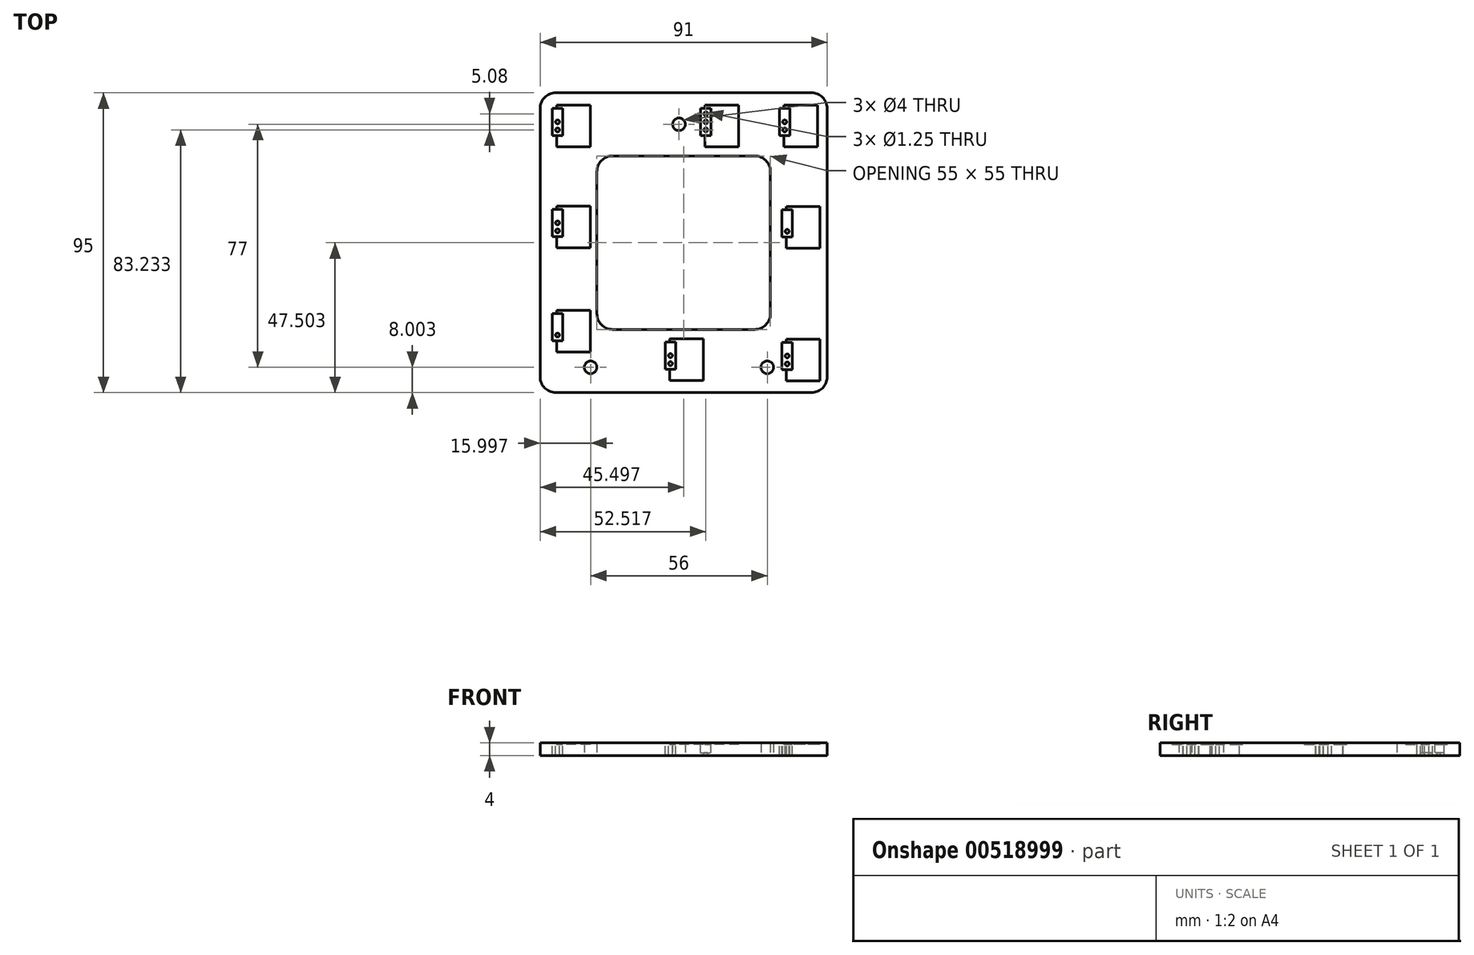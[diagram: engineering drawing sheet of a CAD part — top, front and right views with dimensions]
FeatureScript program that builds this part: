
annotation { "Feature Type Name" : "Feature", "Feature Type Description" : "" }
export const myFeature = defineFeature(function(context is Context, id is Id, definition is map)
    precondition{}
    {
        {
            var Q0;
            Q0=qCreatedBy(makeId("Top.planeOp"),FACE);
            var sketch = newSketch(context, id + "F0", { "sketchPlane" : qUnion([Q0])});
            skLineSegment(sketch, "E0.bottom", {"start": v(-14.66, 9.36) * mm, "end": v(40.34, 9.36) * mm});
            skLineSegment(sketch, "E0.top", {"start": v(-14.66, -45.64) * mm, "end": v(40.34, -45.64) * mm});
            skLineSegment(sketch, "E0.left", {"start": v(-14.66, 9.36) * mm, "end": v(-14.66, -45.64) * mm});
            skLineSegment(sketch, "E0.right", {"start": v(40.34, 9.36) * mm, "end": v(40.34, -45.64) * mm});
            skLineSegment(sketch, "E1.bottom", {"start": v(-32.66, 29.36) * mm, "end": v(58.34, 29.36) * mm});
            skLineSegment(sketch, "E1.top", {"start": v(-32.66, -65.64) * mm, "end": v(58.34, -65.64) * mm});
            skLineSegment(sketch, "E1.left", {"start": v(-32.66, 29.36) * mm, "end": v(-32.66, -65.64) * mm});
            skLineSegment(sketch, "E1.right", {"start": v(58.34, 29.36) * mm, "end": v(58.34, -65.64) * mm});
            skLineSegment(sketch, "E2", {"start": v(40.34, 13.7) * mm, "end": v(58.34, 13.7) * mm, "construction": true});
            skLineSegment(sketch, "E3", {"start": v(-14.66, -14.15) * mm, "end": v(-32.66, -14.15) * mm, "construction": true});
            skLineSegment(sketch, "E4", {"start": v(9.38, 9.36) * mm, "end": v(9.38, 29.36) * mm, "construction": true});
            skLineSegment(sketch, "E5", {"start": v(10.46, -65.64) * mm, "end": v(10.46, -45.64) * mm, "construction": true});
            skCircle(sketch, "E6", {"center": v(11.34, 19.36) * mm, "radius": 2 * mm});
            skCircle(sketch, "E7", {"center": v(39.34, -57.64) * mm, "radius": 2 * mm});
            skCircle(sketch, "E8", {"center": v(-16.66, -57.64) * mm, "radius": 2 * mm});
            skLineSegment(sketch, "E9", {"start": v(39.34, -57.64) * mm, "end": v(-16.66, -57.64) * mm, "construction": true});
            skLineSegment(sketch, "E10", {"start": v(11.34, 19.36) * mm, "end": v(11.34, 29.36) * mm, "construction": true});
            skLineSegment(sketch, "E11", {"start": v(11.34, 19.36) * mm, "end": v(11.34, 9.36) * mm, "construction": true});
            skLineSegment(sketch, "E12", {"start": v(39.34, -57.64) * mm, "end": v(58.34, -57.64) * mm, "construction": true});
            skSolve(sketch);
        }
        {
            var Q0;
            Q0=makeQuery(id+"F0.imprint","IMPRINT",FACE,{"disambiguationData":[TD([[makeQuery(id+"F0.imprint","IMPRINT",EDGE,{"derivedFrom":sQuery(id+"F0.wireOp",EDGE,"E0.bottom")}),1.0]])]});
            extrude(context, id + "F1", {"entities" : qUnion([Q0]), "depth" : 4 * mm, "offsetDistance" : 25 * mm});
        }
        {
            var Q0;
            Q0=makeQuery(id+"F1.opExtrude","CAP_FACE",FACE,{"disambiguationData":[OSD([sQuery(id+"F0.wireOp",EDGE,"E0.bottom"),sQuery(id+"F0.wireOp",EDGE,"E0.top"),sQuery(id+"F0.wireOp",EDGE,"E0.left"),sQuery(id+"F0.wireOp",EDGE,"E0.right"),sQuery(id+"F0.wireOp",EDGE,"E1.bottom"),sQuery(id+"F0.wireOp",EDGE,"E1.top"),sQuery(id+"F0.wireOp",EDGE,"E1.left"),sQuery(id+"F0.wireOp",EDGE,"E1.right")])],"isStart":false});
            var sketch = newSketch(context, id + "F2", { "sketchPlane" : qUnion([Q0])});
            skPoint(sketch, "E13", {"position": v(49.94, 18.86) * mm});
            skLineSegment(sketch, "E14", {"start": v(49.94, 18.86) * mm, "end": v(49.94, 9.36) * mm, "construction": true});
            skLineSegment(sketch, "E15.bottom", {"start": v(55.27, 12.26) * mm, "end": v(44.6, 12.26) * mm});
            skLineSegment(sketch, "E15.top", {"start": v(55.27, 25.47) * mm, "end": v(44.6, 25.47) * mm});
            skLineSegment(sketch, "E15.left", {"start": v(55.27, 12.26) * mm, "end": v(55.27, 25.47) * mm});
            skLineSegment(sketch, "E15.right", {"start": v(44.6, 12.26) * mm, "end": v(44.6, 25.47) * mm});
            skLineSegment(sketch, "E16.bottom", {"start": v(43.2, 24.45) * mm, "end": v(46.5, 24.45) * mm});
            skLineSegment(sketch, "E16.top", {"start": v(43.2, 15.81) * mm, "end": v(46.5, 15.81) * mm});
            skLineSegment(sketch, "E16.left", {"start": v(43.2, 24.45) * mm, "end": v(43.2, 15.81) * mm});
            skLineSegment(sketch, "E16.right", {"start": v(46.5, 24.45) * mm, "end": v(46.5, 15.81) * mm});
            skPoint(sketch, "E17", {"position": v(55.02, 22.67) * mm});
            skPoint(sketch, "E18", {"position": v(52.48, 25.21) * mm});
            skPoint(sketch, "E19", {"position": v(47.4, 25.21) * mm});
            skPoint(sketch, "E20", {"position": v(55.02, 20.13) * mm});
            skPoint(sketch, "E21", {"position": v(55.02, 17.6) * mm});
            skPoint(sketch, "E22", {"position": v(52.48, 12.51) * mm});
            skPoint(sketch, "E23", {"position": v(47.4, 12.51) * mm});
            skPoint(sketch, "E24", {"position": v(44.86, 17.6) * mm});
            skPoint(sketch, "E25", {"position": v(44.86, 22.67) * mm});
            skPoint(sketch, "E26", {"position": v(44.86, 20.13) * mm});
            skLineSegment(sketch, "E27", {"start": v(55.02, 17.6) * mm, "end": v(55.02, 20.13) * mm, "construction": true});
            skLineSegment(sketch, "E28", {"start": v(55.02, 22.67) * mm, "end": v(55.02, 20.13) * mm, "construction": true});
            skLineSegment(sketch, "E29", {"start": v(52.48, 12.51) * mm, "end": v(47.4, 12.51) * mm, "construction": true});
            skLineSegment(sketch, "E30", {"start": v(47.4, 25.21) * mm, "end": v(52.48, 25.21) * mm, "construction": true});
            skLineSegment(sketch, "E31", {"start": v(44.86, 20.13) * mm, "end": v(44.86, 17.6) * mm, "construction": true});
            skLineSegment(sketch, "E32", {"start": v(44.86, 22.67) * mm, "end": v(44.86, 20.13) * mm, "construction": true});
            skLineSegment(sketch, "E33", {"start": v(49.94, 25.21) * mm, "end": v(49.94, 25.47) * mm, "construction": true});
            skPoint(sketch, "E34", {"position": v(44.86, 15.05) * mm});
            skPoint(sketch, "E35", {"position": v(55.02, 15.05) * mm});
            skLineSegment(sketch, "E36", {"start": v(44.86, 17.6) * mm, "end": v(44.86, 15.05) * mm, "construction": true});
            skLineSegment(sketch, "E37", {"start": v(55.02, 17.6) * mm, "end": v(55.02, 15.05) * mm, "construction": true});
            skLineSegment(sketch, "E38", {"start": v(44.86, 18.86) * mm, "end": v(44.6, 18.86) * mm, "construction": true});
            skLineSegment(sketch, "E39", {"start": v(44.86, 22.67) * mm, "end": v(46.5, 22.67) * mm, "construction": true});
            skLineSegment(sketch, "E40", {"start": v(44.86, 22.67) * mm, "end": v(44.86, 24.45) * mm, "construction": true});
            skPoint(sketch, "E40.endSnap0", {"position": v(44.86, 24.45) * mm});
            skLineSegment(sketch, "E41", {"start": v(44.86, 22.67) * mm, "end": v(43.2, 22.67) * mm, "construction": true});
            skCircle(sketch, "E42", {"center": v(44.86, 22.67) * mm, "radius": 0.62 * mm});
            skCircle(sketch, "E43", {"center": v(44.86, 20.13) * mm, "radius": 0.62 * mm});
            skCircle(sketch, "E44", {"center": v(44.86, 17.6) * mm, "radius": 0.62 * mm});
            skLineSegment(sketch, "E45", {"start": v(44.86, 17.6) * mm, "end": v(46.5, 17.6) * mm, "construction": true});
            skLineSegment(sketch, "E46.1.0.0", {"start": v(30.27, 25.47) * mm, "end": v(19.6, 25.47) * mm});
            skLineSegment(sketch, "E46.1.0.1", {"start": v(18.2, 24.45) * mm, "end": v(21.5, 24.45) * mm});
            skCircle(sketch, "E46.1.0.2", {"center": v(19.86, 20.13) * mm, "radius": 0.62 * mm});
            skCircle(sketch, "E46.1.0.3", {"center": v(19.86, 22.67) * mm, "radius": 0.62 * mm});
            skCircle(sketch, "E46.1.0.4", {"center": v(19.86, 17.6) * mm, "radius": 0.62 * mm});
            skLineSegment(sketch, "E46.1.0.5", {"start": v(18.2, 24.45) * mm, "end": v(18.2, 15.81) * mm});
            skLineSegment(sketch, "E46.1.0.6", {"start": v(18.2, 15.81) * mm, "end": v(21.5, 15.81) * mm});
            skLineSegment(sketch, "E46.1.0.7", {"start": v(21.5, 24.45) * mm, "end": v(21.5, 15.81) * mm});
            skLineSegment(sketch, "E46.1.0.8", {"start": v(19.6, 12.26) * mm, "end": v(19.6, 25.47) * mm});
            skLineSegment(sketch, "E46.1.0.9", {"start": v(30.27, 12.26) * mm, "end": v(19.6, 12.26) * mm});
            skLineSegment(sketch, "E46.1.0.10", {"start": v(30.27, 12.26) * mm, "end": v(30.27, 25.47) * mm});
            skLineSegment(sketch, "E46.direction1", {"start": v(44.6, 12.26) * mm, "end": v(19.6, 12.26) * mm, "construction": true});
            skLineSegment(sketch, "E47.1.0.0", {"start": v(-28.8, 24.45) * mm, "end": v(-28.8, 15.81) * mm});
            skLineSegment(sketch, "E47.1.0.1", {"start": v(-27.4, 12.26) * mm, "end": v(-27.4, 25.47) * mm});
            skLineSegment(sketch, "E47.1.0.2", {"start": v(-28.8, 24.45) * mm, "end": v(-25.5, 24.45) * mm});
            skLineSegment(sketch, "E47.1.0.3", {"start": v(-16.73, 12.26) * mm, "end": v(-16.73, 25.47) * mm});
            skLineSegment(sketch, "E47.1.0.4", {"start": v(-28.8, 15.81) * mm, "end": v(-25.5, 15.81) * mm});
            skLineSegment(sketch, "E47.1.0.5", {"start": v(-25.5, 24.45) * mm, "end": v(-25.5, 15.81) * mm});
            skLineSegment(sketch, "E47.1.0.6", {"start": v(-16.73, 25.47) * mm, "end": v(-27.4, 25.47) * mm});
            skLineSegment(sketch, "E47.1.0.7", {"start": v(-16.73, 12.26) * mm, "end": v(-27.4, 12.26) * mm});
            skCircle(sketch, "E47.1.0.8", {"center": v(-27.14, 17.6) * mm, "radius": 0.62 * mm});
            skCircle(sketch, "E47.1.0.9", {"center": v(-27.14, 22.67) * mm, "radius": 0.62 * mm});
            skCircle(sketch, "E47.1.0.10", {"center": v(-27.14, 20.13) * mm, "radius": 0.62 * mm});
            skLineSegment(sketch, "E47.direction1", {"start": v(19.6, 12.26) * mm, "end": v(-27.4, 12.26) * mm, "construction": true});
            skLineSegment(sketch, "E48", {"start": v(49.94, 18.86) * mm, "end": v(58.34, 18.86) * mm, "construction": true});
            skLineSegment(sketch, "E49.0.1.0", {"start": v(-25.5, -7.54) * mm, "end": v(-25.5, -16.17) * mm});
            skLineSegment(sketch, "E49.0.1.1", {"start": v(-16.73, -19.73) * mm, "end": v(-16.73, -6.52) * mm});
            skLineSegment(sketch, "E49.0.1.2", {"start": v(-16.73, -6.52) * mm, "end": v(-27.4, -6.52) * mm});
            skLineSegment(sketch, "E49.0.1.3", {"start": v(-28.8, -16.17) * mm, "end": v(-25.5, -16.17) * mm});
            skLineSegment(sketch, "E49.0.1.4", {"start": v(-16.73, -19.73) * mm, "end": v(-27.4, -19.73) * mm});
            skLineSegment(sketch, "E49.0.1.5", {"start": v(-27.4, -19.73) * mm, "end": v(-27.4, -6.52) * mm});
            skLineSegment(sketch, "E49.0.1.6", {"start": v(-28.8, -7.54) * mm, "end": v(-28.8, -16.17) * mm});
            skCircle(sketch, "E49.0.1.7", {"center": v(-27.14, -9.32) * mm, "radius": 0.62 * mm});
            skCircle(sketch, "E49.0.1.8", {"center": v(-27.14, -14.4) * mm, "radius": 0.62 * mm});
            skCircle(sketch, "E49.0.1.9", {"center": v(-27.14, -11.86) * mm, "radius": 0.62 * mm});
            skLineSegment(sketch, "E49.0.1.10", {"start": v(-28.8, -7.54) * mm, "end": v(-25.5, -7.54) * mm});
            skLineSegment(sketch, "E49.direction1", {"start": v(-26.4, 12.26) * mm, "end": v(-7.4, 12.5) * mm, "construction": true});
            skLineSegment(sketch, "E49.direction2", {"start": v(-26.4, 12.26) * mm, "end": v(-26.4, -19.74) * mm, "construction": true});
            skLineSegment(sketch, "E50.0.1.0", {"start": v(-16.73, -52.74) * mm, "end": v(-16.73, -39.53) * mm});
            skLineSegment(sketch, "E50.0.1.1", {"start": v(-28.8, -40.55) * mm, "end": v(-28.8, -49.19) * mm});
            skLineSegment(sketch, "E50.0.1.2", {"start": v(-25.5, -40.55) * mm, "end": v(-25.5, -49.19) * mm});
            skLineSegment(sketch, "E50.0.1.3", {"start": v(-27.4, -52.74) * mm, "end": v(-27.4, -39.53) * mm});
            skLineSegment(sketch, "E50.0.1.4", {"start": v(-16.73, -39.53) * mm, "end": v(-27.4, -39.53) * mm});
            skLineSegment(sketch, "E50.0.1.5", {"start": v(-16.73, -52.74) * mm, "end": v(-27.4, -52.74) * mm});
            skCircle(sketch, "E50.0.1.6", {"center": v(-27.14, -47.4) * mm, "radius": 0.62 * mm});
            skCircle(sketch, "E50.0.1.7", {"center": v(-27.14, -42.33) * mm, "radius": 0.62 * mm});
            skCircle(sketch, "E50.0.1.8", {"center": v(-27.14, -44.87) * mm, "radius": 0.62 * mm});
            skLineSegment(sketch, "E50.0.1.9", {"start": v(-28.8, -49.19) * mm, "end": v(-25.5, -49.19) * mm});
            skLineSegment(sketch, "E50.0.1.10", {"start": v(-28.8, -40.55) * mm, "end": v(-25.5, -40.55) * mm});
            skLineSegment(sketch, "E50.direction1", {"start": v(-27.4, 12.26) * mm, "end": v(-2.4, 12.26) * mm, "construction": true});
            skLineSegment(sketch, "E50.direction2", {"start": v(-27.4, 12.26) * mm, "end": v(-27.4, -52.74) * mm, "construction": true});
            skLineSegment(sketch, "E51.1.0.0", {"start": v(7, -58.24) * mm, "end": v(10.3, -58.24) * mm});
            skLineSegment(sketch, "E51.1.0.1", {"start": v(8.4, -61.8) * mm, "end": v(8.4, -48.6) * mm});
            skLineSegment(sketch, "E51.1.0.2", {"start": v(19.07, -48.6) * mm, "end": v(8.4, -48.6) * mm});
            skLineSegment(sketch, "E51.1.0.3", {"start": v(19.07, -61.8) * mm, "end": v(8.4, -61.8) * mm});
            skLineSegment(sketch, "E51.1.0.4", {"start": v(19.07, -61.8) * mm, "end": v(19.07, -48.6) * mm});
            skLineSegment(sketch, "E51.1.0.5", {"start": v(7, -49.6) * mm, "end": v(7, -58.24) * mm});
            skLineSegment(sketch, "E51.1.0.6", {"start": v(10.3, -49.6) * mm, "end": v(10.3, -58.24) * mm});
            skCircle(sketch, "E51.1.0.7", {"center": v(8.65, -56.47) * mm, "radius": 0.62 * mm});
            skCircle(sketch, "E51.1.0.8", {"center": v(8.65, -53.93) * mm, "radius": 0.62 * mm});
            skCircle(sketch, "E51.1.0.9", {"center": v(8.65, -51.39) * mm, "radius": 0.62 * mm});
            skLineSegment(sketch, "E51.1.0.10", {"start": v(7, -49.6) * mm, "end": v(10.3, -49.6) * mm});
            skLineSegment(sketch, "E51.direction1", {"start": v(-27.4, -52.74) * mm, "end": v(8.4, -61.8) * mm, "construction": true});
            skLineSegment(sketch, "E52.1.0.0", {"start": v(56.07, -61.9) * mm, "end": v(45.4, -61.9) * mm});
            skLineSegment(sketch, "E52.1.0.1", {"start": v(44, -58.34) * mm, "end": v(47.3, -58.34) * mm});
            skLineSegment(sketch, "E52.1.0.2", {"start": v(47.3, -49.7) * mm, "end": v(47.3, -58.34) * mm});
            skLineSegment(sketch, "E52.1.0.3", {"start": v(45.4, -61.9) * mm, "end": v(45.4, -48.7) * mm});
            skLineSegment(sketch, "E52.1.0.4", {"start": v(56.07, -48.7) * mm, "end": v(45.4, -48.7) * mm});
            skLineSegment(sketch, "E52.1.0.5", {"start": v(56.07, -61.9) * mm, "end": v(56.07, -48.7) * mm});
            skLineSegment(sketch, "E52.1.0.6", {"start": v(44, -49.7) * mm, "end": v(44, -58.34) * mm});
            skCircle(sketch, "E52.1.0.7", {"center": v(45.65, -51.49) * mm, "radius": 0.62 * mm});
            skCircle(sketch, "E52.1.0.8", {"center": v(45.65, -56.57) * mm, "radius": 0.62 * mm});
            skCircle(sketch, "E52.1.0.9", {"center": v(45.65, -54.03) * mm, "radius": 0.62 * mm});
            skLineSegment(sketch, "E52.1.0.10", {"start": v(44, -49.7) * mm, "end": v(47.3, -49.7) * mm});
            skLineSegment(sketch, "E52.direction1", {"start": v(8.4, -61.8) * mm, "end": v(45.4, -61.9) * mm, "construction": true});
            skLineSegment(sketch, "E53.0.1.0", {"start": v(47.3, -7.7) * mm, "end": v(47.3, -16.34) * mm});
            skLineSegment(sketch, "E53.0.1.1", {"start": v(44, -7.7) * mm, "end": v(44, -16.34) * mm});
            skLineSegment(sketch, "E53.0.1.2", {"start": v(56.07, -19.9) * mm, "end": v(56.07, -6.7) * mm});
            skLineSegment(sketch, "E53.0.1.3", {"start": v(56.07, -6.7) * mm, "end": v(45.4, -6.7) * mm});
            skLineSegment(sketch, "E53.0.1.4", {"start": v(45.4, -19.9) * mm, "end": v(45.4, -6.7) * mm});
            skLineSegment(sketch, "E53.0.1.5", {"start": v(56.07, -19.9) * mm, "end": v(45.4, -19.9) * mm});
            skLineSegment(sketch, "E53.0.1.6", {"start": v(44, -16.34) * mm, "end": v(47.3, -16.34) * mm});
            skCircle(sketch, "E53.0.1.7", {"center": v(45.65, -9.49) * mm, "radius": 0.62 * mm});
            skCircle(sketch, "E53.0.1.8", {"center": v(45.65, -14.57) * mm, "radius": 0.62 * mm});
            skCircle(sketch, "E53.0.1.9", {"center": v(45.65, -12.03) * mm, "radius": 0.62 * mm});
            skLineSegment(sketch, "E53.0.1.10", {"start": v(44, -7.7) * mm, "end": v(47.3, -7.7) * mm});
            skLineSegment(sketch, "E53.direction1", {"start": v(45.4, -61.9) * mm, "end": v(70.4, -62) * mm, "construction": true});
            skLineSegment(sketch, "E53.direction2", {"start": v(45.4, -61.9) * mm, "end": v(45.4, -19.9) * mm, "construction": true});
            skSolve(sketch);
        }
        {
            var Q0;
            Q0 = qSketchRegion(id + "F2", true);
            extrude(context, id + "F3", {"entities" : qUnion([Q0]), "operationType" : NewBodyOperationType.REMOVE, "oppositeDirection" : true, "depth" : 0.5 * mm, "offsetDistance" : 25 * mm});
        }
        {
            var Q0;
            {var subQ5=sQuery(id+"F2.wireOp",EDGE,"E16.left");Q0=makeQuery(id+"F2.imprint","IMPRINT",FACE,{"disambiguationData":[TD([[makeQuery(id+"F2.imprint","IMPRINT",EDGE,{"derivedFrom":subQ5}),1.0]])]});}
            var Q1;
            {var subQ5=sQuery(id+"F2.wireOp",EDGE,"E16.right");Q1=makeQuery(id+"F2.imprint","IMPRINT",FACE,{"disambiguationData":[TD([[makeQuery(id+"F2.imprint","IMPRINT",EDGE,{"derivedFrom":subQ5}),-1.0]])]});}
            var Q2;
            {var subQ10=sQuery(id+"F2.wireOp",EDGE,"E46.1.0.7");Q2=makeQuery(id+"F2.imprint","IMPRINT",FACE,{"disambiguationData":[TD([[makeQuery(id+"F2.imprint","IMPRINT",EDGE,{"derivedFrom":subQ10}),-1.0]])]});}
            var Q3;
            {var subQ12=sQuery(id+"F2.wireOp",EDGE,"E46.1.0.5");Q3=makeQuery(id+"F2.imprint","IMPRINT",FACE,{"disambiguationData":[TD([[makeQuery(id+"F2.imprint","IMPRINT",EDGE,{"derivedFrom":subQ12}),1.0]])]});}
            var Q4;
            {var subQ11=sQuery(id+"F2.wireOp",EDGE,"E53.0.1.0");Q4=makeQuery(id+"F2.imprint","IMPRINT",FACE,{"disambiguationData":[TD([[makeQuery(id+"F2.imprint","IMPRINT",EDGE,{"derivedFrom":subQ11}),-1.0]])]});}
            var Q5;
            {var subQ12=sQuery(id+"F2.wireOp",EDGE,"E53.0.1.1");Q5=makeQuery(id+"F2.imprint","IMPRINT",FACE,{"disambiguationData":[TD([[makeQuery(id+"F2.imprint","IMPRINT",EDGE,{"derivedFrom":subQ12}),1.0]])]});}
            var Q6;
            {var subQ5=sQuery(id+"F2.wireOp",EDGE,"E52.1.0.2");Q6=makeQuery(id+"F2.imprint","IMPRINT",FACE,{"disambiguationData":[TD([[makeQuery(id+"F2.imprint","IMPRINT",EDGE,{"derivedFrom":subQ5}),-1.0]])]});}
            var Q7;
            {var subQ12=sQuery(id+"F2.wireOp",EDGE,"E52.1.0.6");Q7=makeQuery(id+"F2.imprint","IMPRINT",FACE,{"disambiguationData":[TD([[makeQuery(id+"F2.imprint","IMPRINT",EDGE,{"derivedFrom":subQ12}),1.0]])]});}
            var Q8;
            {var subQ11=sQuery(id+"F2.wireOp",EDGE,"E51.1.0.6");Q8=makeQuery(id+"F2.imprint","IMPRINT",FACE,{"disambiguationData":[TD([[makeQuery(id+"F2.imprint","IMPRINT",EDGE,{"derivedFrom":subQ11}),-1.0]])]});}
            var Q9;
            {var subQ10=sQuery(id+"F2.wireOp",EDGE,"E51.1.0.5");Q9=makeQuery(id+"F2.imprint","IMPRINT",FACE,{"disambiguationData":[TD([[makeQuery(id+"F2.imprint","IMPRINT",EDGE,{"derivedFrom":subQ10}),1.0]])]});}
            var Q10;
            {var subQ12=sQuery(id+"F2.wireOp",EDGE,"E50.0.1.2");Q10=makeQuery(id+"F2.imprint","IMPRINT",FACE,{"disambiguationData":[TD([[makeQuery(id+"F2.imprint","IMPRINT",EDGE,{"derivedFrom":subQ12}),-1.0]])]});}
            var Q11;
            {var subQ11=sQuery(id+"F2.wireOp",EDGE,"E50.0.1.1");Q11=makeQuery(id+"F2.imprint","IMPRINT",FACE,{"disambiguationData":[TD([[makeQuery(id+"F2.imprint","IMPRINT",EDGE,{"derivedFrom":subQ11}),1.0]])]});}
            var Q12;
            {var subQ8=sQuery(id+"F2.wireOp",EDGE,"E49.0.1.0");Q12=makeQuery(id+"F2.imprint","IMPRINT",FACE,{"disambiguationData":[TD([[makeQuery(id+"F2.imprint","IMPRINT",EDGE,{"derivedFrom":subQ8}),-1.0]])]});}
            var Q13;
            {var subQ6=sQuery(id+"F2.wireOp",EDGE,"E49.0.1.6");Q13=makeQuery(id+"F2.imprint","IMPRINT",FACE,{"disambiguationData":[TD([[makeQuery(id+"F2.imprint","IMPRINT",EDGE,{"derivedFrom":subQ6}),1.0]])]});}
            var Q14;
            {var subQ12=sQuery(id+"F2.wireOp",EDGE,"E47.1.0.5");Q14=makeQuery(id+"F2.imprint","IMPRINT",FACE,{"disambiguationData":[TD([[makeQuery(id+"F2.imprint","IMPRINT",EDGE,{"derivedFrom":subQ12}),-1.0]])]});}
            var Q15;
            {var subQ11=sQuery(id+"F2.wireOp",EDGE,"E47.1.0.0");Q15=makeQuery(id+"F2.imprint","IMPRINT",FACE,{"disambiguationData":[TD([[makeQuery(id+"F2.imprint","IMPRINT",EDGE,{"derivedFrom":subQ11}),1.0]])]});}
            extrude(context, id + "F4", {"entities" : qUnion([Q0, Q1, Q2, Q3, Q4, Q5, Q6, Q7, Q8, Q9, Q10, Q11, Q12, Q13, Q14, Q15]), "operationType" : NewBodyOperationType.REMOVE, "oppositeDirection" : true, "depth" : 3.2 * mm, "offsetDistance" : 25 * mm});
        }
        {
            var Q0;
            {var subQ0=sQuery(id+"F2.wireOp",EDGE,"E42");var subQ1=sQuery(id+"F2.wireOp",EDGE,"E15.right");var subQ2=makeQuery(id+"F2.imprint","INTERSECT",VERTEX,{"disambiguationData":[OD(0.0)],"derivedFrom":[subQ1,subQ0]});Q0=makeQuery(id+"F2.imprint","IMPRINT",FACE,{"disambiguationData":[TD([[makeQuery(id+"F2.imprint","IMPRINT",EDGE,{"disambiguationData":[TD([[subQ2,-1.0]])],"derivedFrom":subQ1}),-1.0]])]});}
            var Q1;
            {var subQ0=sQuery(id+"F2.wireOp",EDGE,"E42");var subQ1=sQuery(id+"F2.wireOp",EDGE,"E15.right");var subQ2=makeQuery(id+"F2.imprint","INTERSECT",VERTEX,{"disambiguationData":[OD(0.0)],"derivedFrom":[subQ1,subQ0]});Q1=makeQuery(id+"F2.imprint","IMPRINT",FACE,{"disambiguationData":[TD([[makeQuery(id+"F2.imprint","IMPRINT",EDGE,{"disambiguationData":[TD([[subQ2,-1.0]])],"derivedFrom":subQ1}),1.0]])]});}
            var Q2;
            {var subQ0=sQuery(id+"F2.wireOp",EDGE,"E43");var subQ1=sQuery(id+"F2.wireOp",EDGE,"E15.right");var subQ2=makeQuery(id+"F2.imprint","INTERSECT",VERTEX,{"disambiguationData":[OD(0.0)],"derivedFrom":[subQ1,subQ0]});Q2=makeQuery(id+"F2.imprint","IMPRINT",FACE,{"disambiguationData":[TD([[makeQuery(id+"F2.imprint","IMPRINT",EDGE,{"disambiguationData":[TD([[subQ2,-1.0]])],"derivedFrom":subQ1}),-1.0]])]});}
            var Q3;
            {var subQ0=sQuery(id+"F2.wireOp",EDGE,"E43");var subQ1=sQuery(id+"F2.wireOp",EDGE,"E15.right");var subQ2=makeQuery(id+"F2.imprint","INTERSECT",VERTEX,{"disambiguationData":[OD(0.0)],"derivedFrom":[subQ1,subQ0]});Q3=makeQuery(id+"F2.imprint","IMPRINT",FACE,{"disambiguationData":[TD([[makeQuery(id+"F2.imprint","IMPRINT",EDGE,{"disambiguationData":[TD([[subQ2,-1.0]])],"derivedFrom":subQ1}),1.0]])]});}
            var Q4;
            {var subQ0=sQuery(id+"F2.wireOp",EDGE,"E44");var subQ1=sQuery(id+"F2.wireOp",EDGE,"E15.right");var subQ2=makeQuery(id+"F2.imprint","INTERSECT",VERTEX,{"disambiguationData":[OD(0.0)],"derivedFrom":[subQ1,subQ0]});Q4=makeQuery(id+"F2.imprint","IMPRINT",FACE,{"disambiguationData":[TD([[makeQuery(id+"F2.imprint","IMPRINT",EDGE,{"disambiguationData":[TD([[subQ2,-1.0]])],"derivedFrom":subQ1}),-1.0]])]});}
            var Q5;
            {var subQ0=sQuery(id+"F2.wireOp",EDGE,"E44");var subQ1=sQuery(id+"F2.wireOp",EDGE,"E15.right");var subQ2=makeQuery(id+"F2.imprint","INTERSECT",VERTEX,{"disambiguationData":[OD(0.0)],"derivedFrom":[subQ1,subQ0]});Q5=makeQuery(id+"F2.imprint","IMPRINT",FACE,{"disambiguationData":[TD([[makeQuery(id+"F2.imprint","IMPRINT",EDGE,{"disambiguationData":[TD([[subQ2,-1.0]])],"derivedFrom":subQ1}),1.0]])]});}
            var Q6;
            {var subQ0=sQuery(id+"F2.wireOp",EDGE,"E46.1.0.8");var subQ1=sQuery(id+"F2.wireOp",EDGE,"E46.1.0.3");var subQ2=makeQuery(id+"F2.imprint","INTERSECT",VERTEX,{"disambiguationData":[OD(0.0)],"derivedFrom":[subQ1,subQ0]});Q6=makeQuery(id+"F2.imprint","IMPRINT",FACE,{"disambiguationData":[TD([[makeQuery(id+"F2.imprint","IMPRINT",EDGE,{"disambiguationData":[TD([[subQ2,-1.0]])],"derivedFrom":subQ1}),1.0]])]});}
            var Q7;
            {var subQ0=sQuery(id+"F2.wireOp",EDGE,"E46.1.0.8");var subQ1=sQuery(id+"F2.wireOp",EDGE,"E46.1.0.3");var subQ2=makeQuery(id+"F2.imprint","INTERSECT",VERTEX,{"disambiguationData":[OD(0.0)],"derivedFrom":[subQ1,subQ0]});Q7=makeQuery(id+"F2.imprint","IMPRINT",FACE,{"disambiguationData":[TD([[makeQuery(id+"F2.imprint","IMPRINT",EDGE,{"disambiguationData":[TD([[subQ2,1.0]])],"derivedFrom":subQ1}),1.0]])]});}
            var Q8;
            {var subQ0=sQuery(id+"F2.wireOp",EDGE,"E46.1.0.8");var subQ1=sQuery(id+"F2.wireOp",EDGE,"E46.1.0.2");var subQ2=makeQuery(id+"F2.imprint","INTERSECT",VERTEX,{"disambiguationData":[OD(0.0)],"derivedFrom":[subQ1,subQ0]});Q8=makeQuery(id+"F2.imprint","IMPRINT",FACE,{"disambiguationData":[TD([[makeQuery(id+"F2.imprint","IMPRINT",EDGE,{"disambiguationData":[TD([[subQ2,-1.0]])],"derivedFrom":subQ1}),1.0]])]});}
            var Q9;
            {var subQ0=sQuery(id+"F2.wireOp",EDGE,"E46.1.0.8");var subQ1=sQuery(id+"F2.wireOp",EDGE,"E46.1.0.2");var subQ2=makeQuery(id+"F2.imprint","INTERSECT",VERTEX,{"disambiguationData":[OD(0.0)],"derivedFrom":[subQ1,subQ0]});Q9=makeQuery(id+"F2.imprint","IMPRINT",FACE,{"disambiguationData":[TD([[makeQuery(id+"F2.imprint","IMPRINT",EDGE,{"disambiguationData":[TD([[subQ2,1.0]])],"derivedFrom":subQ1}),1.0]])]});}
            var Q10;
            {var subQ0=sQuery(id+"F2.wireOp",EDGE,"E46.1.0.8");var subQ1=sQuery(id+"F2.wireOp",EDGE,"E46.1.0.4");var subQ2=makeQuery(id+"F2.imprint","INTERSECT",VERTEX,{"disambiguationData":[OD(0.0)],"derivedFrom":[subQ1,subQ0]});Q10=makeQuery(id+"F2.imprint","IMPRINT",FACE,{"disambiguationData":[TD([[makeQuery(id+"F2.imprint","IMPRINT",EDGE,{"disambiguationData":[TD([[subQ2,-1.0]])],"derivedFrom":subQ1}),1.0]])]});}
            var Q11;
            {var subQ0=sQuery(id+"F2.wireOp",EDGE,"E46.1.0.8");var subQ1=sQuery(id+"F2.wireOp",EDGE,"E46.1.0.4");var subQ2=makeQuery(id+"F2.imprint","INTERSECT",VERTEX,{"disambiguationData":[OD(0.0)],"derivedFrom":[subQ1,subQ0]});Q11=makeQuery(id+"F2.imprint","IMPRINT",FACE,{"disambiguationData":[TD([[makeQuery(id+"F2.imprint","IMPRINT",EDGE,{"disambiguationData":[TD([[subQ2,1.0]])],"derivedFrom":subQ1}),1.0]])]});}
            var Q12;
            {var subQ0=sQuery(id+"F2.wireOp",EDGE,"E47.1.0.9");var subQ1=sQuery(id+"F2.wireOp",EDGE,"E47.1.0.1");var subQ2=makeQuery(id+"F2.imprint","INTERSECT",VERTEX,{"disambiguationData":[OD(0.0)],"derivedFrom":[subQ1,subQ0]});Q12=makeQuery(id+"F2.imprint","IMPRINT",FACE,{"disambiguationData":[TD([[makeQuery(id+"F2.imprint","IMPRINT",EDGE,{"disambiguationData":[TD([[subQ2,-1.0]])],"derivedFrom":subQ1}),-1.0]])]});}
            var Q13;
            {var subQ0=sQuery(id+"F2.wireOp",EDGE,"E47.1.0.9");var subQ1=sQuery(id+"F2.wireOp",EDGE,"E47.1.0.1");var subQ2=makeQuery(id+"F2.imprint","INTERSECT",VERTEX,{"disambiguationData":[OD(0.0)],"derivedFrom":[subQ1,subQ0]});Q13=makeQuery(id+"F2.imprint","IMPRINT",FACE,{"disambiguationData":[TD([[makeQuery(id+"F2.imprint","IMPRINT",EDGE,{"disambiguationData":[TD([[subQ2,-1.0]])],"derivedFrom":subQ1}),1.0]])]});}
            var Q14;
            {var subQ0=sQuery(id+"F2.wireOp",EDGE,"E47.1.0.10");var subQ1=sQuery(id+"F2.wireOp",EDGE,"E47.1.0.1");var subQ2=makeQuery(id+"F2.imprint","INTERSECT",VERTEX,{"disambiguationData":[OD(0.0)],"derivedFrom":[subQ1,subQ0]});Q14=makeQuery(id+"F2.imprint","IMPRINT",FACE,{"disambiguationData":[TD([[makeQuery(id+"F2.imprint","IMPRINT",EDGE,{"disambiguationData":[TD([[subQ2,-1.0]])],"derivedFrom":subQ1}),-1.0]])]});}
            var Q15;
            {var subQ0=sQuery(id+"F2.wireOp",EDGE,"E47.1.0.10");var subQ1=sQuery(id+"F2.wireOp",EDGE,"E47.1.0.1");var subQ2=makeQuery(id+"F2.imprint","INTERSECT",VERTEX,{"disambiguationData":[OD(0.0)],"derivedFrom":[subQ1,subQ0]});Q15=makeQuery(id+"F2.imprint","IMPRINT",FACE,{"disambiguationData":[TD([[makeQuery(id+"F2.imprint","IMPRINT",EDGE,{"disambiguationData":[TD([[subQ2,-1.0]])],"derivedFrom":subQ1}),1.0]])]});}
            var Q16;
            {var subQ0=sQuery(id+"F2.wireOp",EDGE,"E47.1.0.8");var subQ1=sQuery(id+"F2.wireOp",EDGE,"E47.1.0.1");var subQ2=makeQuery(id+"F2.imprint","INTERSECT",VERTEX,{"disambiguationData":[OD(0.0)],"derivedFrom":[subQ1,subQ0]});Q16=makeQuery(id+"F2.imprint","IMPRINT",FACE,{"disambiguationData":[TD([[makeQuery(id+"F2.imprint","IMPRINT",EDGE,{"disambiguationData":[TD([[subQ2,-1.0]])],"derivedFrom":subQ1}),-1.0]])]});}
            var Q17;
            {var subQ0=sQuery(id+"F2.wireOp",EDGE,"E47.1.0.8");var subQ1=sQuery(id+"F2.wireOp",EDGE,"E47.1.0.1");var subQ2=makeQuery(id+"F2.imprint","INTERSECT",VERTEX,{"disambiguationData":[OD(0.0)],"derivedFrom":[subQ1,subQ0]});Q17=makeQuery(id+"F2.imprint","IMPRINT",FACE,{"disambiguationData":[TD([[makeQuery(id+"F2.imprint","IMPRINT",EDGE,{"disambiguationData":[TD([[subQ2,-1.0]])],"derivedFrom":subQ1}),1.0]])]});}
            var Q18;
            {var subQ0=sQuery(id+"F2.wireOp",EDGE,"E49.0.1.7");var subQ1=sQuery(id+"F2.wireOp",EDGE,"E49.0.1.5");var subQ2=makeQuery(id+"F2.imprint","INTERSECT",VERTEX,{"disambiguationData":[OD(0.0)],"derivedFrom":[subQ1,subQ0]});Q18=makeQuery(id+"F2.imprint","IMPRINT",FACE,{"disambiguationData":[TD([[makeQuery(id+"F2.imprint","IMPRINT",EDGE,{"disambiguationData":[TD([[subQ2,-1.0]])],"derivedFrom":subQ1}),1.0]])]});}
            var Q19;
            {var subQ0=sQuery(id+"F2.wireOp",EDGE,"E49.0.1.7");var subQ1=sQuery(id+"F2.wireOp",EDGE,"E49.0.1.5");var subQ2=makeQuery(id+"F2.imprint","INTERSECT",VERTEX,{"disambiguationData":[OD(0.0)],"derivedFrom":[subQ1,subQ0]});Q19=makeQuery(id+"F2.imprint","IMPRINT",FACE,{"disambiguationData":[TD([[makeQuery(id+"F2.imprint","IMPRINT",EDGE,{"disambiguationData":[TD([[subQ2,-1.0]])],"derivedFrom":subQ1}),-1.0]])]});}
            var Q20;
            {var subQ0=sQuery(id+"F2.wireOp",EDGE,"E49.0.1.9");var subQ1=sQuery(id+"F2.wireOp",EDGE,"E49.0.1.5");var subQ2=makeQuery(id+"F2.imprint","INTERSECT",VERTEX,{"disambiguationData":[OD(0.0)],"derivedFrom":[subQ1,subQ0]});Q20=makeQuery(id+"F2.imprint","IMPRINT",FACE,{"disambiguationData":[TD([[makeQuery(id+"F2.imprint","IMPRINT",EDGE,{"disambiguationData":[TD([[subQ2,-1.0]])],"derivedFrom":subQ1}),-1.0]])]});}
            var Q21;
            {var subQ0=sQuery(id+"F2.wireOp",EDGE,"E49.0.1.9");var subQ1=sQuery(id+"F2.wireOp",EDGE,"E49.0.1.5");var subQ2=makeQuery(id+"F2.imprint","INTERSECT",VERTEX,{"disambiguationData":[OD(0.0)],"derivedFrom":[subQ1,subQ0]});Q21=makeQuery(id+"F2.imprint","IMPRINT",FACE,{"disambiguationData":[TD([[makeQuery(id+"F2.imprint","IMPRINT",EDGE,{"disambiguationData":[TD([[subQ2,-1.0]])],"derivedFrom":subQ1}),1.0]])]});}
            var Q22;
            {var subQ0=sQuery(id+"F2.wireOp",EDGE,"E49.0.1.8");var subQ1=sQuery(id+"F2.wireOp",EDGE,"E49.0.1.5");var subQ2=makeQuery(id+"F2.imprint","INTERSECT",VERTEX,{"disambiguationData":[OD(0.0)],"derivedFrom":[subQ1,subQ0]});Q22=makeQuery(id+"F2.imprint","IMPRINT",FACE,{"disambiguationData":[TD([[makeQuery(id+"F2.imprint","IMPRINT",EDGE,{"disambiguationData":[TD([[subQ2,-1.0]])],"derivedFrom":subQ1}),-1.0]])]});}
            var Q23;
            {var subQ0=sQuery(id+"F2.wireOp",EDGE,"E49.0.1.8");var subQ1=sQuery(id+"F2.wireOp",EDGE,"E49.0.1.5");var subQ2=makeQuery(id+"F2.imprint","INTERSECT",VERTEX,{"disambiguationData":[OD(0.0)],"derivedFrom":[subQ1,subQ0]});Q23=makeQuery(id+"F2.imprint","IMPRINT",FACE,{"disambiguationData":[TD([[makeQuery(id+"F2.imprint","IMPRINT",EDGE,{"disambiguationData":[TD([[subQ2,-1.0]])],"derivedFrom":subQ1}),1.0]])]});}
            var Q24;
            {var subQ0=sQuery(id+"F2.wireOp",EDGE,"E50.0.1.7");var subQ1=sQuery(id+"F2.wireOp",EDGE,"E50.0.1.3");var subQ2=makeQuery(id+"F2.imprint","INTERSECT",VERTEX,{"disambiguationData":[OD(0.0)],"derivedFrom":[subQ1,subQ0]});Q24=makeQuery(id+"F2.imprint","IMPRINT",FACE,{"disambiguationData":[TD([[makeQuery(id+"F2.imprint","IMPRINT",EDGE,{"disambiguationData":[TD([[subQ2,-1.0]])],"derivedFrom":subQ1}),-1.0]])]});}
            var Q25;
            {var subQ0=sQuery(id+"F2.wireOp",EDGE,"E50.0.1.7");var subQ1=sQuery(id+"F2.wireOp",EDGE,"E50.0.1.3");var subQ2=makeQuery(id+"F2.imprint","INTERSECT",VERTEX,{"disambiguationData":[OD(0.0)],"derivedFrom":[subQ1,subQ0]});Q25=makeQuery(id+"F2.imprint","IMPRINT",FACE,{"disambiguationData":[TD([[makeQuery(id+"F2.imprint","IMPRINT",EDGE,{"disambiguationData":[TD([[subQ2,-1.0]])],"derivedFrom":subQ1}),1.0]])]});}
            var Q26;
            {var subQ0=sQuery(id+"F2.wireOp",EDGE,"E50.0.1.8");var subQ1=sQuery(id+"F2.wireOp",EDGE,"E50.0.1.3");var subQ2=makeQuery(id+"F2.imprint","INTERSECT",VERTEX,{"disambiguationData":[OD(0.0)],"derivedFrom":[subQ1,subQ0]});Q26=makeQuery(id+"F2.imprint","IMPRINT",FACE,{"disambiguationData":[TD([[makeQuery(id+"F2.imprint","IMPRINT",EDGE,{"disambiguationData":[TD([[subQ2,-1.0]])],"derivedFrom":subQ1}),-1.0]])]});}
            var Q27;
            {var subQ0=sQuery(id+"F2.wireOp",EDGE,"E50.0.1.8");var subQ1=sQuery(id+"F2.wireOp",EDGE,"E50.0.1.3");var subQ2=makeQuery(id+"F2.imprint","INTERSECT",VERTEX,{"disambiguationData":[OD(0.0)],"derivedFrom":[subQ1,subQ0]});Q27=makeQuery(id+"F2.imprint","IMPRINT",FACE,{"disambiguationData":[TD([[makeQuery(id+"F2.imprint","IMPRINT",EDGE,{"disambiguationData":[TD([[subQ2,-1.0]])],"derivedFrom":subQ1}),1.0]])]});}
            var Q28;
            {var subQ0=sQuery(id+"F2.wireOp",EDGE,"E50.0.1.6");var subQ1=sQuery(id+"F2.wireOp",EDGE,"E50.0.1.3");var subQ2=makeQuery(id+"F2.imprint","INTERSECT",VERTEX,{"disambiguationData":[OD(0.0)],"derivedFrom":[subQ1,subQ0]});Q28=makeQuery(id+"F2.imprint","IMPRINT",FACE,{"disambiguationData":[TD([[makeQuery(id+"F2.imprint","IMPRINT",EDGE,{"disambiguationData":[TD([[subQ2,-1.0]])],"derivedFrom":subQ1}),-1.0]])]});}
            var Q29;
            {var subQ0=sQuery(id+"F2.wireOp",EDGE,"E50.0.1.6");var subQ1=sQuery(id+"F2.wireOp",EDGE,"E50.0.1.3");var subQ2=makeQuery(id+"F2.imprint","INTERSECT",VERTEX,{"disambiguationData":[OD(0.0)],"derivedFrom":[subQ1,subQ0]});Q29=makeQuery(id+"F2.imprint","IMPRINT",FACE,{"disambiguationData":[TD([[makeQuery(id+"F2.imprint","IMPRINT",EDGE,{"disambiguationData":[TD([[subQ2,-1.0]])],"derivedFrom":subQ1}),1.0]])]});}
            var Q30;
            {var subQ0=sQuery(id+"F2.wireOp",EDGE,"E51.1.0.9");var subQ1=sQuery(id+"F2.wireOp",EDGE,"E51.1.0.1");var subQ2=makeQuery(id+"F2.imprint","INTERSECT",VERTEX,{"disambiguationData":[OD(0.0)],"derivedFrom":[subQ1,subQ0]});Q30=makeQuery(id+"F2.imprint","IMPRINT",FACE,{"disambiguationData":[TD([[makeQuery(id+"F2.imprint","IMPRINT",EDGE,{"disambiguationData":[TD([[subQ2,-1.0]])],"derivedFrom":subQ1}),-1.0]])]});}
            var Q31;
            {var subQ0=sQuery(id+"F2.wireOp",EDGE,"E51.1.0.9");var subQ1=sQuery(id+"F2.wireOp",EDGE,"E51.1.0.1");var subQ2=makeQuery(id+"F2.imprint","INTERSECT",VERTEX,{"disambiguationData":[OD(0.0)],"derivedFrom":[subQ1,subQ0]});Q31=makeQuery(id+"F2.imprint","IMPRINT",FACE,{"disambiguationData":[TD([[makeQuery(id+"F2.imprint","IMPRINT",EDGE,{"disambiguationData":[TD([[subQ2,-1.0]])],"derivedFrom":subQ1}),1.0]])]});}
            var Q32;
            {var subQ0=sQuery(id+"F2.wireOp",EDGE,"E51.1.0.8");var subQ1=sQuery(id+"F2.wireOp",EDGE,"E51.1.0.1");var subQ2=makeQuery(id+"F2.imprint","INTERSECT",VERTEX,{"disambiguationData":[OD(0.0)],"derivedFrom":[subQ1,subQ0]});Q32=makeQuery(id+"F2.imprint","IMPRINT",FACE,{"disambiguationData":[TD([[makeQuery(id+"F2.imprint","IMPRINT",EDGE,{"disambiguationData":[TD([[subQ2,-1.0]])],"derivedFrom":subQ1}),-1.0]])]});}
            var Q33;
            {var subQ0=sQuery(id+"F2.wireOp",EDGE,"E51.1.0.8");var subQ1=sQuery(id+"F2.wireOp",EDGE,"E51.1.0.1");var subQ2=makeQuery(id+"F2.imprint","INTERSECT",VERTEX,{"disambiguationData":[OD(0.0)],"derivedFrom":[subQ1,subQ0]});Q33=makeQuery(id+"F2.imprint","IMPRINT",FACE,{"disambiguationData":[TD([[makeQuery(id+"F2.imprint","IMPRINT",EDGE,{"disambiguationData":[TD([[subQ2,-1.0]])],"derivedFrom":subQ1}),1.0]])]});}
            var Q34;
            {var subQ0=sQuery(id+"F2.wireOp",EDGE,"E51.1.0.7");var subQ1=sQuery(id+"F2.wireOp",EDGE,"E51.1.0.1");var subQ2=makeQuery(id+"F2.imprint","INTERSECT",VERTEX,{"disambiguationData":[OD(0.0)],"derivedFrom":[subQ1,subQ0]});Q34=makeQuery(id+"F2.imprint","IMPRINT",FACE,{"disambiguationData":[TD([[makeQuery(id+"F2.imprint","IMPRINT",EDGE,{"disambiguationData":[TD([[subQ2,-1.0]])],"derivedFrom":subQ1}),-1.0]])]});}
            var Q35;
            {var subQ0=sQuery(id+"F2.wireOp",EDGE,"E51.1.0.7");var subQ1=sQuery(id+"F2.wireOp",EDGE,"E51.1.0.1");var subQ2=makeQuery(id+"F2.imprint","INTERSECT",VERTEX,{"disambiguationData":[OD(0.0)],"derivedFrom":[subQ1,subQ0]});Q35=makeQuery(id+"F2.imprint","IMPRINT",FACE,{"disambiguationData":[TD([[makeQuery(id+"F2.imprint","IMPRINT",EDGE,{"disambiguationData":[TD([[subQ2,-1.0]])],"derivedFrom":subQ1}),1.0]])]});}
            var Q36;
            {var subQ0=sQuery(id+"F2.wireOp",EDGE,"E52.1.0.7");var subQ1=sQuery(id+"F2.wireOp",EDGE,"E52.1.0.3");var subQ2=makeQuery(id+"F2.imprint","INTERSECT",VERTEX,{"disambiguationData":[OD(0.0)],"derivedFrom":[subQ1,subQ0]});Q36=makeQuery(id+"F2.imprint","IMPRINT",FACE,{"disambiguationData":[TD([[makeQuery(id+"F2.imprint","IMPRINT",EDGE,{"disambiguationData":[TD([[subQ2,-1.0]])],"derivedFrom":subQ1}),-1.0]])]});}
            var Q37;
            {var subQ0=sQuery(id+"F2.wireOp",EDGE,"E52.1.0.7");var subQ1=sQuery(id+"F2.wireOp",EDGE,"E52.1.0.3");var subQ2=makeQuery(id+"F2.imprint","INTERSECT",VERTEX,{"disambiguationData":[OD(0.0)],"derivedFrom":[subQ1,subQ0]});Q37=makeQuery(id+"F2.imprint","IMPRINT",FACE,{"disambiguationData":[TD([[makeQuery(id+"F2.imprint","IMPRINT",EDGE,{"disambiguationData":[TD([[subQ2,-1.0]])],"derivedFrom":subQ1}),1.0]])]});}
            var Q38;
            {var subQ0=sQuery(id+"F2.wireOp",EDGE,"E52.1.0.9");var subQ1=sQuery(id+"F2.wireOp",EDGE,"E52.1.0.3");var subQ2=makeQuery(id+"F2.imprint","INTERSECT",VERTEX,{"disambiguationData":[OD(0.0)],"derivedFrom":[subQ1,subQ0]});Q38=makeQuery(id+"F2.imprint","IMPRINT",FACE,{"disambiguationData":[TD([[makeQuery(id+"F2.imprint","IMPRINT",EDGE,{"disambiguationData":[TD([[subQ2,-1.0]])],"derivedFrom":subQ1}),-1.0]])]});}
            var Q39;
            {var subQ0=sQuery(id+"F2.wireOp",EDGE,"E52.1.0.9");var subQ1=sQuery(id+"F2.wireOp",EDGE,"E52.1.0.3");var subQ2=makeQuery(id+"F2.imprint","INTERSECT",VERTEX,{"disambiguationData":[OD(0.0)],"derivedFrom":[subQ1,subQ0]});Q39=makeQuery(id+"F2.imprint","IMPRINT",FACE,{"disambiguationData":[TD([[makeQuery(id+"F2.imprint","IMPRINT",EDGE,{"disambiguationData":[TD([[subQ2,-1.0]])],"derivedFrom":subQ1}),1.0]])]});}
            var Q40;
            {var subQ0=sQuery(id+"F2.wireOp",EDGE,"E52.1.0.8");var subQ1=sQuery(id+"F2.wireOp",EDGE,"E52.1.0.3");var subQ2=makeQuery(id+"F2.imprint","INTERSECT",VERTEX,{"disambiguationData":[OD(0.0)],"derivedFrom":[subQ1,subQ0]});Q40=makeQuery(id+"F2.imprint","IMPRINT",FACE,{"disambiguationData":[TD([[makeQuery(id+"F2.imprint","IMPRINT",EDGE,{"disambiguationData":[TD([[subQ2,-1.0]])],"derivedFrom":subQ1}),-1.0]])]});}
            var Q41;
            {var subQ0=sQuery(id+"F2.wireOp",EDGE,"E52.1.0.8");var subQ1=sQuery(id+"F2.wireOp",EDGE,"E52.1.0.3");var subQ2=makeQuery(id+"F2.imprint","INTERSECT",VERTEX,{"disambiguationData":[OD(0.0)],"derivedFrom":[subQ1,subQ0]});Q41=makeQuery(id+"F2.imprint","IMPRINT",FACE,{"disambiguationData":[TD([[makeQuery(id+"F2.imprint","IMPRINT",EDGE,{"disambiguationData":[TD([[subQ2,-1.0]])],"derivedFrom":subQ1}),1.0]])]});}
            var Q42;
            {var subQ0=sQuery(id+"F2.wireOp",EDGE,"E53.0.1.8");var subQ1=sQuery(id+"F2.wireOp",EDGE,"E53.0.1.4");var subQ2=makeQuery(id+"F2.imprint","INTERSECT",VERTEX,{"disambiguationData":[OD(0.0)],"derivedFrom":[subQ1,subQ0]});Q42=makeQuery(id+"F2.imprint","IMPRINT",FACE,{"disambiguationData":[TD([[makeQuery(id+"F2.imprint","IMPRINT",EDGE,{"disambiguationData":[TD([[subQ2,-1.0]])],"derivedFrom":subQ1}),-1.0]])]});}
            var Q43;
            {var subQ0=sQuery(id+"F2.wireOp",EDGE,"E53.0.1.8");var subQ1=sQuery(id+"F2.wireOp",EDGE,"E53.0.1.4");var subQ2=makeQuery(id+"F2.imprint","INTERSECT",VERTEX,{"disambiguationData":[OD(0.0)],"derivedFrom":[subQ1,subQ0]});Q43=makeQuery(id+"F2.imprint","IMPRINT",FACE,{"disambiguationData":[TD([[makeQuery(id+"F2.imprint","IMPRINT",EDGE,{"disambiguationData":[TD([[subQ2,-1.0]])],"derivedFrom":subQ1}),1.0]])]});}
            var Q44;
            {var subQ0=sQuery(id+"F2.wireOp",EDGE,"E53.0.1.9");var subQ1=sQuery(id+"F2.wireOp",EDGE,"E53.0.1.4");var subQ2=makeQuery(id+"F2.imprint","INTERSECT",VERTEX,{"disambiguationData":[OD(0.0)],"derivedFrom":[subQ1,subQ0]});Q44=makeQuery(id+"F2.imprint","IMPRINT",FACE,{"disambiguationData":[TD([[makeQuery(id+"F2.imprint","IMPRINT",EDGE,{"disambiguationData":[TD([[subQ2,-1.0]])],"derivedFrom":subQ1}),-1.0]])]});}
            var Q45;
            {var subQ0=sQuery(id+"F2.wireOp",EDGE,"E53.0.1.9");var subQ1=sQuery(id+"F2.wireOp",EDGE,"E53.0.1.4");var subQ2=makeQuery(id+"F2.imprint","INTERSECT",VERTEX,{"disambiguationData":[OD(0.0)],"derivedFrom":[subQ1,subQ0]});Q45=makeQuery(id+"F2.imprint","IMPRINT",FACE,{"disambiguationData":[TD([[makeQuery(id+"F2.imprint","IMPRINT",EDGE,{"disambiguationData":[TD([[subQ2,-1.0]])],"derivedFrom":subQ1}),1.0]])]});}
            var Q46;
            {var subQ0=sQuery(id+"F2.wireOp",EDGE,"E53.0.1.7");var subQ1=sQuery(id+"F2.wireOp",EDGE,"E53.0.1.4");var subQ2=makeQuery(id+"F2.imprint","INTERSECT",VERTEX,{"disambiguationData":[OD(0.0)],"derivedFrom":[subQ1,subQ0]});Q46=makeQuery(id+"F2.imprint","IMPRINT",FACE,{"disambiguationData":[TD([[makeQuery(id+"F2.imprint","IMPRINT",EDGE,{"disambiguationData":[TD([[subQ2,-1.0]])],"derivedFrom":subQ1}),-1.0]])]});}
            var Q47;
            {var subQ0=sQuery(id+"F2.wireOp",EDGE,"E53.0.1.7");var subQ1=sQuery(id+"F2.wireOp",EDGE,"E53.0.1.4");var subQ2=makeQuery(id+"F2.imprint","INTERSECT",VERTEX,{"disambiguationData":[OD(0.0)],"derivedFrom":[subQ1,subQ0]});Q47=makeQuery(id+"F2.imprint","IMPRINT",FACE,{"disambiguationData":[TD([[makeQuery(id+"F2.imprint","IMPRINT",EDGE,{"disambiguationData":[TD([[subQ2,-1.0]])],"derivedFrom":subQ1}),1.0]])]});}
            extrude(context, id + "F5", {"entities" : qUnion([Q0, Q1, Q2, Q3, Q4, Q5, Q6, Q7, Q8, Q9, Q10, Q11, Q12, Q13, Q14, Q15, Q16, Q17, Q18, Q19, Q20, Q21, Q22, Q23, Q24, Q25, Q26, Q27, Q28, Q29, Q30, Q31, Q32, Q33, Q34, Q35, Q36, Q37, Q38, Q39, Q40, Q41, Q42, Q43, Q44, Q45, Q46, Q47]), "operationType" : NewBodyOperationType.REMOVE, "oppositeDirection" : true, "depth" : 25 * mm, "offsetDistance" : 25 * mm});
        }
        {
            var Q0;
            {var subQ7=sQuery(id+"F2.wireOp",EDGE,"E15.bottom");Q0=makeQuery(id+"F2.imprint","IMPRINT",FACE,{"disambiguationData":[TD([[makeQuery(id+"F2.imprint","IMPRINT",EDGE,{"derivedFrom":subQ7}),1.0]])]});}
            var sketch = newSketch(context, id + "F6", { "sketchPlane" : qUnion([Q0])});
            skLineSegment(sketch, "E54.bottom", {"start": v(14.32, 35.1) * mm, "end": v(-58.72, 35.1) * mm});
            skLineSegment(sketch, "E54.top", {"start": v(14.32, -71.58) * mm, "end": v(-58.72, -71.58) * mm});
            skLineSegment(sketch, "E54.left", {"start": v(14.32, 35.1) * mm, "end": v(14.32, -71.58) * mm});
            skLineSegment(sketch, "E54.right", {"start": v(-58.72, 35.1) * mm, "end": v(-58.72, -71.58) * mm});
            skLineSegment(sketch, "E55.bottom", {"start": v(33.1, 35.77) * mm, "end": v(76.1, 35.77) * mm});
            skLineSegment(sketch, "E55.top", {"start": v(33.1, -75.33) * mm, "end": v(76.1, -75.33) * mm});
            skLineSegment(sketch, "E55.left", {"start": v(33.1, 35.77) * mm, "end": v(33.1, -75.33) * mm});
            skLineSegment(sketch, "E55.right", {"start": v(76.1, 35.77) * mm, "end": v(76.1, -75.33) * mm});
            skLineSegment(sketch, "E56.bottom", {"start": v(2.72, -23.45) * mm, "end": v(49.65, -23.45) * mm});
            skLineSegment(sketch, "E56.top", {"start": v(2.72, -79.43) * mm, "end": v(49.65, -79.43) * mm});
            skLineSegment(sketch, "E56.left", {"start": v(2.72, -23.45) * mm, "end": v(2.72, -79.43) * mm});
            skLineSegment(sketch, "E56.right", {"start": v(49.65, -23.45) * mm, "end": v(49.65, -79.43) * mm});
            skSolve(sketch);
        }
        {
            var Q0;
            Q0=makeQuery(id+"F1.opExtrude","SWEPT_EDGE",EDGE,{"disambiguationData":[OSD([sQuery(id+"F0.wireOp",EDGE,"E0.bottom"),sQuery(id+"F0.wireOp",EDGE,"E0.left")])]});
            var Q1;
            Q1=makeQuery(id+"F1.opExtrude","SWEPT_EDGE",EDGE,{"disambiguationData":[OSD([sQuery(id+"F0.wireOp",EDGE,"E0.bottom"),sQuery(id+"F0.wireOp",EDGE,"E0.right")])]});
            var Q2;
            Q2=makeQuery(id+"F1.opExtrude","SWEPT_EDGE",EDGE,{"disambiguationData":[OSD([sQuery(id+"F0.wireOp",EDGE,"E0.top"),sQuery(id+"F0.wireOp",EDGE,"E0.left")])]});
            var Q3;
            Q3=makeQuery(id+"F1.opExtrude","SWEPT_EDGE",EDGE,{"disambiguationData":[OSD([sQuery(id+"F0.wireOp",EDGE,"E0.top"),sQuery(id+"F0.wireOp",EDGE,"E0.right")])]});
            var Q4;
            Q4=makeQuery(id+"F1.opExtrude","SWEPT_EDGE",EDGE,{"disambiguationData":[OSD([sQuery(id+"F0.wireOp",EDGE,"E1.top"),sQuery(id+"F0.wireOp",EDGE,"E1.right")])]});
            var Q5;
            Q5=makeQuery(id+"F1.opExtrude","SWEPT_EDGE",EDGE,{"disambiguationData":[OSD([sQuery(id+"F0.wireOp",EDGE,"E1.top"),sQuery(id+"F0.wireOp",EDGE,"E1.left")])]});
            var Q6;
            Q6=makeQuery(id+"F1.opExtrude","SWEPT_EDGE",EDGE,{"disambiguationData":[OSD([sQuery(id+"F0.wireOp",EDGE,"E1.bottom"),sQuery(id+"F0.wireOp",EDGE,"E1.left")])]});
            var Q7;
            Q7=makeQuery(id+"F1.opExtrude","SWEPT_EDGE",EDGE,{"disambiguationData":[OSD([sQuery(id+"F0.wireOp",EDGE,"E1.bottom"),sQuery(id+"F0.wireOp",EDGE,"E1.right")])]});
            fillet(context, id + "F7", {"entities" : qUnion([Q0, Q1, Q2, Q3, Q4, Q5, Q6, Q7]), "radius" : 5 * mm, "tangentPropagation" : true, "allowEdgeOverflow" : false});
        }
    });
